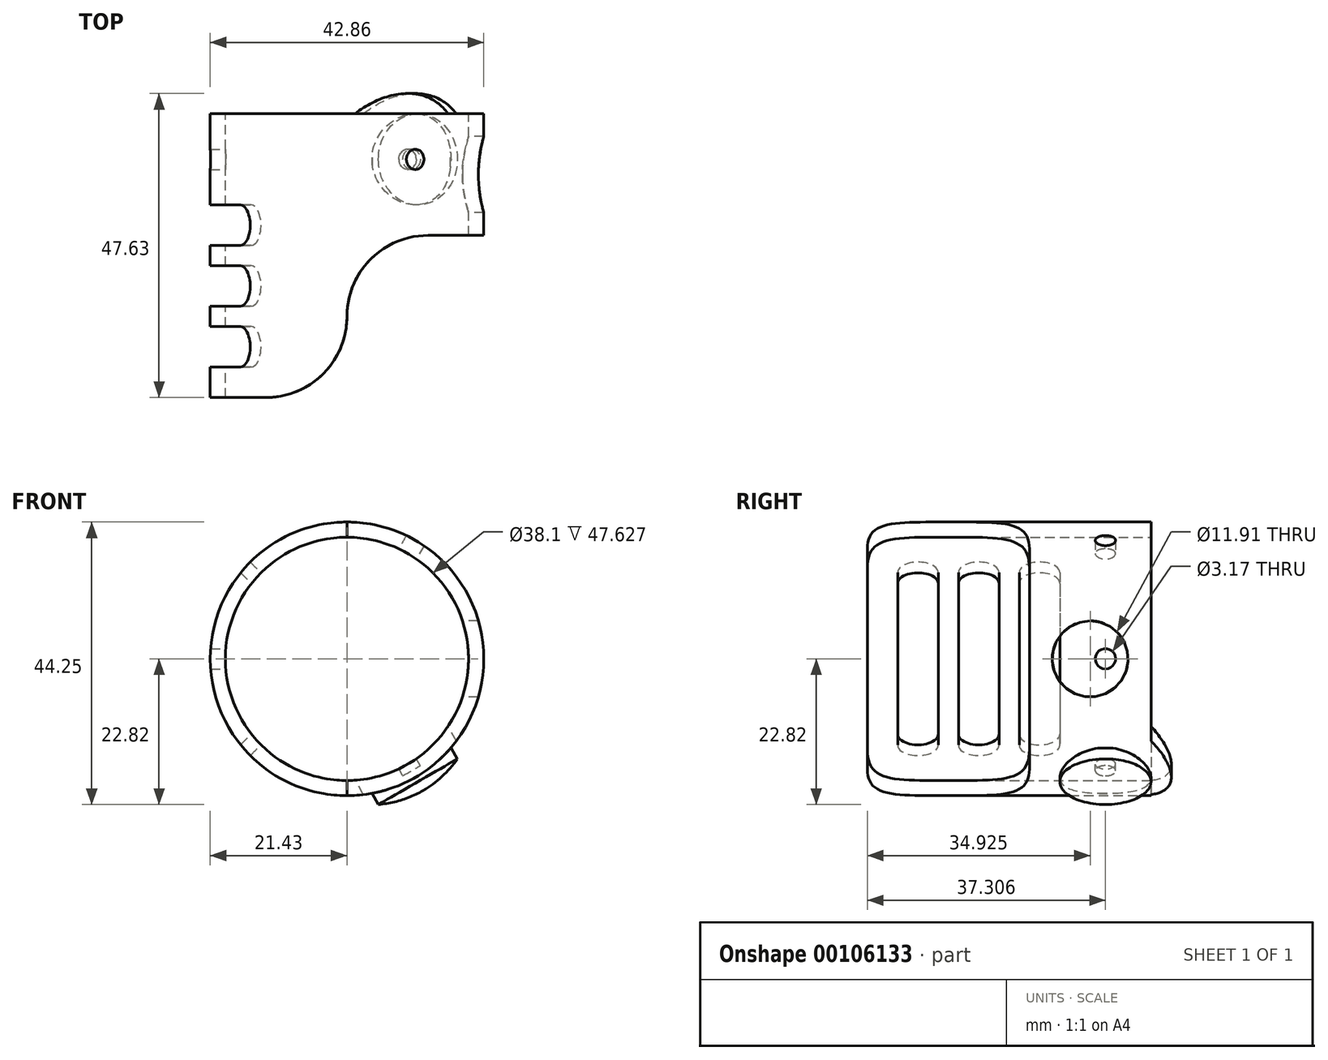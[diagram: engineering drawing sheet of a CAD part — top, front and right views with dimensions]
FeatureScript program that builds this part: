
annotation { "Feature Type Name" : "Feature", "Feature Type Description" : "" }
export const myFeature = defineFeature(function(context is Context, id is Id, definition is map)
    precondition{}
    {
        {
            var Q0;
            Q0=qCreatedBy(makeId("Right.planeOp"),FACE);
            var sketch = newSketch(context, id + "F0", { "sketchPlane" : qUnion([Q0])});
            skLineSegment(sketch, "E0", {"start": v(0, 0) * mm, "end": v(-152.4, 0) * mm, "construction": true});
            skLineSegment(sketch, "E1.bottom", {"start": v(-95.25, 21.43) * mm, "end": v(-47.63, 21.43) * mm});
            skLineSegment(sketch, "E1.top", {"start": v(-95.25, 19.05) * mm, "end": v(-47.63, 19.05) * mm});
            skLineSegment(sketch, "E1.left", {"start": v(-95.25, 21.43) * mm, "end": v(-95.25, 19.05) * mm});
            skLineSegment(sketch, "E1.right", {"start": v(-47.63, 21.43) * mm, "end": v(-47.63, 19.05) * mm});
            skSolve(sketch);
        }
        {
            var Q0;
            Q0 = qSketchRegion(id + "F0", true);
            var Q1;
            Q1=sQuery(id+"F0.wireOp",EDGE,"E0");
            revolve(context, id + "F1", {"entities" : qUnion([Q0]), "axis" : qUnion([Q1]), "revolveType" : RevolveType.FULL});
        }
        {
            var Q0;
            Q0=qCreatedBy(makeId("Top.planeOp"),FACE);
            var sketch = newSketch(context, id + "F2", { "sketchPlane" : qUnion([Q0])});
            skLineSegment(sketch, "E2", {"start": v(0, -95.25) * mm, "end": v(0, -82.55) * mm, "construction": true});
            skLineSegment(sketch, "E3", {"start": v(0, -82.55) * mm, "end": v(-12.7, -82.55) * mm, "construction": true});
            skArc(sketch, "E4", {"start": v(-12.7, -95.25) * mm, "mid": v(-3.72, -91.53) * mm, "end": v(0, -82.55) * mm});
            skLineSegment(sketch, "E5", {"start": v(-12.7, -95.25) * mm, "end": v(21.43, -95.25) * mm});
            skLineSegment(sketch, "E6", {"start": v(21.43, -95.25) * mm, "end": v(21.43, -69.85) * mm});
            skArc(sketch, "E7.MirrorC", {"start": v(0, -82.55) * mm, "mid": v(3.72, -73.57) * mm, "end": v(12.7, -69.85) * mm});
            skLineSegment(sketch, "E8", {"start": v(21.43, -69.85) * mm, "end": v(12.7, -69.85) * mm});
            skSolve(sketch);
        }
        {
            var Q0;
            Q0 = qSketchRegion(id + "F2", true);
            extrude(context, id + "F3", {"entities" : qUnion([Q0]), "operationType" : NewBodyOperationType.REMOVE, "endBound" : BoundingType.THROUGH_ALL, "oppositeDirection" : true, "depth" : 21.43 * mm, "hasSecondDirection" : true, "secondDirectionBound" : BoundingType.THROUGH_ALL, "secondDirectionOppositeDirection" : false, "secondDirectionDepth" : 25.4 * mm});
        }
        {
            var Q0;
            Q0=qCreatedBy(makeId("Right.planeOp"),FACE);
            var sketch = newSketch(context, id + "F4", { "sketchPlane" : qUnion([Q0])});
            skLineSegment(sketch, "E9", {"start": v(0, 0) * mm, "end": v(-60.32, 0) * mm, "construction": true});
            skCircle(sketch, "E10", {"center": v(-60.32, 0) * mm, "radius": 5.95 * mm});
            skSolve(sketch);
        }
        {
            var Q0;
            Q0 = qSketchRegion(id + "F4", true);
            var Q1;
            Q1=makeQuery(id+"F1.opRevolve","SWEPT_FACE",FACE,{"disambiguationData":[OSD([sQuery(id+"F0.wireOp",EDGE,"E1.bottom")])]});
            extrude(context, id + "F5", {"entities" : qUnion([Q0]), "operationType" : NewBodyOperationType.REMOVE, "endBound" : BoundingType.UP_TO_SURFACE, "endBoundEntityFace" : qUnion([Q1]), "depth" : 25.4 * mm});
        }
        {
            var Q0;
            Q0=qCreatedBy(makeId("Right.planeOp"),FACE);
            var sketch = newSketch(context, id + "F6", { "sketchPlane" : qUnion([Q0])});
            skLineSegment(sketch, "E11", {"start": v(0, 0) * mm, "end": v(-57.94, 0) * mm, "construction": true});
            skCircle(sketch, "E12", {"center": v(-57.94, 0) * mm, "radius": 1.59 * mm});
            skSolve(sketch);
        }
        {
            var Q0;
            Q0 = qSketchRegion(id + "F6", true);
            var Q1;
            Q1=makeQuery(id+"F1.opRevolve","SWEPT_FACE",FACE,{"disambiguationData":[OSD([sQuery(id+"F0.wireOp",EDGE,"E1.bottom")])]});
            extrude(context, id + "F7", {"entities" : qUnion([Q0]), "operationType" : NewBodyOperationType.REMOVE, "endBound" : BoundingType.UP_TO_SURFACE, "oppositeDirection" : true, "endBoundEntityFace" : qUnion([Q1]), "depth" : 25.4 * mm});
        }
        {
            var Q0;
            Q0=qCreatedBy(makeId("Front.planeOp"),FACE);
            var sketch = newSketch(context, id + "F8", { "sketchPlane" : qUnion([Q0])});
            skLineSegment(sketch, "E13", {"start": v(-21.43, 0) * mm, "end": v(21.43, 0) * mm, "construction": true});
            skLineSegment(sketch, "E14", {"start": v(0, 21.43) * mm, "end": v(0, -21.43) * mm, "construction": true});
            skLineSegment(sketch, "E15", {"start": v(-18.56, -10.72) * mm, "end": v(18.56, 10.72) * mm, "construction": true});
            skLineSegment(sketch, "E16.MirrorCS", {"start": v(18.56, -10.72) * mm, "end": v(-18.56, 10.72) * mm, "construction": true});
            skSolve(sketch);
        }
        {
            var Q0;
            Q0=sQuery(id+"F8.wireOp",VERTEX,"E15.end");
            var Q1;
            Q1=sQuery(id+"F8.wireOp",VERTEX,"E15.start");
            var Q2;
            Q2=sQuery(id+"F0.wireOp",VERTEX,"E0.end");
            cPlane(context, id + "F9", {"entities" : qUnion([Q0, Q1, Q2]), "cplaneType" : CPlaneType.THREE_POINT, "offset" : 25.4 * mm, "width" : 152.4 * mm, "height" : 152.4 * mm});
        }
        {
            var Q0;
            Q0=sQuery(id+"F8.wireOp",VERTEX,"E16.MirrorCS.end");
            var Q1;
            Q1=sQuery(id+"F8.wireOp",VERTEX,"E16.MirrorCS.start");
            var Q2;
            Q2=sQuery(id+"F0.wireOp",VERTEX,"E0.end");
            cPlane(context, id + "F10", {"entities" : qUnion([Q0, Q1, Q2]), "cplaneType" : CPlaneType.THREE_POINT, "offset" : 25.4 * mm, "width" : 152.4 * mm, "height" : 152.4 * mm});
        }
        {
            var Q0;
            Q0=qCreatedBy(id+"F9.planeOp",FACE);
            var sketch = newSketch(context, id + "F11", { "sketchPlane" : qUnion([Q0])});
            skLineSegment(sketch, "E17", {"start": v(0, 0) * mm, "end": v(0, 57.94) * mm, "construction": true});
            skCircle(sketch, "E18", {"center": v(0, 57.94) * mm, "radius": 1.59 * mm});
            skSolve(sketch);
        }
        {
            var Q0;
            Q0 = qSketchRegion(id + "F11", true);
            var Q1;
            Q1=makeQuery(id+"F1.opRevolve","SWEPT_FACE",FACE,{"disambiguationData":[OSD([sQuery(id+"F0.wireOp",EDGE,"E1.bottom")])]});
            extrude(context, id + "F12", {"entities" : qUnion([Q0]), "operationType" : NewBodyOperationType.REMOVE, "endBound" : BoundingType.UP_TO_SURFACE, "endBoundEntityFace" : qUnion([Q1]), "depth" : 25.4 * mm});
        }
        {
            var Q0;
            Q0=qCreatedBy(id+"F10.planeOp",FACE);
            var sketch = newSketch(context, id + "F13", { "sketchPlane" : qUnion([Q0])});
            skLineSegment(sketch, "E19", {"start": v(0, 0) * mm, "end": v(0, -57.94) * mm, "construction": true});
            skCircle(sketch, "E20", {"center": v(0, -57.94) * mm, "radius": 1.59 * mm});
            skSolve(sketch);
        }
        {
            var Q0;
            Q0 = qSketchRegion(id + "F13", true);
            var Q1;
            Q1=makeQuery(id+"F1.opRevolve","SWEPT_FACE",FACE,{"disambiguationData":[OSD([sQuery(id+"F0.wireOp",EDGE,"E1.bottom")])]});
            extrude(context, id + "F14", {"entities" : qUnion([Q0]), "operationType" : NewBodyOperationType.REMOVE, "endBound" : BoundingType.UP_TO_SURFACE, "endBoundEntityFace" : qUnion([Q1]), "depth" : 25.4 * mm});
        }
        {
            var Q0;
            Q0=qCreatedBy(id+"F9.planeOp",FACE);
            var sketch = newSketch(context, id + "F15", { "sketchPlane" : qUnion([Q0])});
            skLineSegment(sketch, "E21", {"start": v(0, 0) * mm, "end": v(0, 60.32) * mm, "construction": true});
            skArc(sketch, "E22", {"start": v(-8.4, 50.8) * mm, "mid": v(0, 47.62) * mm, "end": v(8.4, 50.8) * mm});
            skLineSegment(sketch, "E23", {"start": v(8.4, 50.8) * mm, "end": v(21.43, 50.8) * mm});
            skLineSegment(sketch, "E24", {"start": v(21.43, 50.8) * mm, "end": v(21.43, 47.63) * mm});
            skLineSegment(sketch, "E25", {"start": v(21.43, 47.63) * mm, "end": v(-21.43, 47.62) * mm});
            skLineSegment(sketch, "E26.MirrorCS", {"start": v(-21.43, 50.8) * mm, "end": v(-21.43, 47.63) * mm});
            skLineSegment(sketch, "E27.MirrorCS", {"start": v(-8.4, 50.8) * mm, "end": v(-21.43, 50.8) * mm});
            skSolve(sketch);
        }
        {
            var Q0;
            Q0 = qSketchRegion(id + "F15", true);
            var Q1;
            Q1=makeQuery(id+"F1.opRevolve","SWEPT_FACE",FACE,{"disambiguationData":[OSD([sQuery(id+"F0.wireOp",EDGE,"E1.bottom")])]});
            extrude(context, id + "F16", {"entities" : qUnion([Q0]), "operationType" : NewBodyOperationType.REMOVE, "endBoundEntityFace" : qUnion([Q1]), "depth" : 21.43 * mm});
        }
        {
            var Q0;
            Q0=qCreatedBy(id+"F9.planeOp",FACE);
            var sketch = newSketch(context, id + "F17", { "sketchPlane" : qUnion([Q0])});
            skLineSegment(sketch, "E28.bottom", {"start": v(21.43, 50.8) * mm, "end": v(-21.43, 50.8) * mm});
            skLineSegment(sketch, "E28.top", {"start": v(21.43, 47.63) * mm, "end": v(-21.43, 47.63) * mm});
            skLineSegment(sketch, "E28.left", {"start": v(21.43, 50.8) * mm, "end": v(21.43, 47.63) * mm});
            skLineSegment(sketch, "E28.right", {"start": v(-21.43, 50.8) * mm, "end": v(-21.43, 47.63) * mm});
            skSolve(sketch);
        }
        {
            var Q0;
            Q0 = qSketchRegion(id + "F17", true);
            extrude(context, id + "F18", {"entities" : qUnion([Q0]), "operationType" : NewBodyOperationType.REMOVE, "oppositeDirection" : true, "depth" : 21.43 * mm});
        }
        {
            var Q0;
            Q0=qCreatedBy(id+"F9.planeOp",FACE);
            cPlane(context, id + "F19", {"entities" : qUnion([Q0]), "cplaneType" : CPlaneType.OFFSET, "offset" : 21.43 * mm, "width" : 152.4 * mm, "height" : 152.4 * mm});
        }
        {
            var Q0;
            Q0=qCreatedBy(id+"F19.planeOp",FACE);
            var sketch = newSketch(context, id + "F20", { "sketchPlane" : qUnion([Q0])});
            skLineSegment(sketch, "E29", {"start": v(0, 0) * mm, "end": v(0, 57.94) * mm, "construction": true});
            skCircle(sketch, "E30", {"center": v(0, 57.94) * mm, "radius": 7.14 * mm});
            skSolve(sketch);
        }
        {
            var Q0;
            Q0 = qSketchRegion(id + "F20", true);
            var Q1;
            Q1=makeQuery(id+"F1.opRevolve","SWEPT_FACE",FACE,{"disambiguationData":[OSD([sQuery(id+"F0.wireOp",EDGE,"E1.bottom")])]});
            extrude(context, id + "F21", {"entities" : qUnion([Q0]), "operationType" : NewBodyOperationType.ADD, "endBoundEntityFace" : qUnion([Q1]), "depth" : 0.8 * mm, "hasSecondDirection" : true, "secondDirectionOppositeDirection" : true, "secondDirectionDepth" : 1.2 * mm});
        }
        {
            var Q0;
            Q0=qCreatedBy(makeId("Front.planeOp"),FACE);
            cPlane(context, id + "F22", {"entities" : qUnion([Q0]), "cplaneType" : CPlaneType.OFFSET, "offset" : 57.94 * mm, "width" : 152.4 * mm, "height" : 152.4 * mm});
        }
        {
            var Q0;
            Q0=qCreatedBy(id+"F22.planeOp",FACE);
            var sketch = newSketch(context, id + "F23", { "sketchPlane" : qUnion([Q0])});
            skLineSegment(sketch, "E31", {"start": v(0, 0) * mm, "end": v(21.43, 0) * mm, "construction": true});
            skLineSegment(sketch, "E32", {"start": v(0, 0) * mm, "end": v(11.11, -19.25) * mm, "construction": true});
            skLineSegment(sketch, "E33", {"start": v(11.11, -19.25) * mm, "end": v(17.3, -15.68) * mm});
            skArc(sketch, "E34", {"start": v(11.92, -20.64) * mm, "mid": v(14.88, -18.46) * mm, "end": v(17.3, -15.68) * mm});
            skLineSegment(sketch, "E35", {"start": v(11.11, -19.25) * mm, "end": v(11.92, -20.64) * mm});
            skSolve(sketch);
        }
        {
            var Q0;
            Q0 = qSketchRegion(id + "F23", true);
            var Q1;
            Q1=sQuery(id+"F23.wireOp",EDGE,"E32");
            revolve(context, id + "F24", {"operationType" : NewBodyOperationType.ADD, "entities" : qUnion([Q0]), "axis" : qUnion([Q1]), "revolveType" : RevolveType.FULL});
        }
        {
            var Q0;
            Q0=qCreatedBy(makeId("Right.planeOp"),FACE);
            cPlane(context, id + "F25", {"entities" : qUnion([Q0]), "cplaneType" : CPlaneType.OFFSET, "offset" : 21.43 * mm, "oppositeDirection" : true, "width" : 152.4 * mm, "height" : 152.4 * mm});
        }
        {
            var Q0;
            Q0=qCreatedBy(makeId("Right.planeOp"),FACE);
            cPlane(context, id + "F26", {"entities" : qUnion([Q0]), "cplaneType" : CPlaneType.OFFSET, "offset" : 8.73 * mm, "oppositeDirection" : true, "width" : 152.4 * mm, "height" : 152.4 * mm});
        }
        {
            var Q0;
            Q0=qCreatedBy(id+"F25.planeOp",FACE);
            var sketch = newSketch(context, id + "F27", { "sketchPlane" : qUnion([Q0])});
            skLineSegment(sketch, "E36", {"start": v(0, 0) * mm, "end": v(-87.31, 0) * mm, "construction": true});
            skLineSegment(sketch, "E37", {"start": v(-87.31, 18.26) * mm, "end": v(-87.31, -18.26) * mm, "construction": true});
            skLineSegment(sketch, "E38", {"start": v(-77.79, 18.26) * mm, "end": v(-77.79, -18.26) * mm, "construction": true});
            skLineSegment(sketch, "E39", {"start": v(-68.26, 18.26) * mm, "end": v(-68.26, -18.26) * mm, "construction": true});
            skArc(sketch, "E40", {"start": v(-84.14, 18.26) * mm, "mid": v(-87.31, 21.43) * mm, "end": v(-90.49, 18.26) * mm});
            skArc(sketch, "E41", {"start": v(-74.61, 18.26) * mm, "mid": v(-77.79, 21.43) * mm, "end": v(-80.96, 18.26) * mm});
            skArc(sketch, "E42", {"start": v(-65.09, 18.26) * mm, "mid": v(-68.26, 21.43) * mm, "end": v(-71.44, 18.26) * mm});
            skArc(sketch, "E43.MirrorC", {"start": v(-65.09, -18.26) * mm, "mid": v(-68.26, -21.43) * mm, "end": v(-71.44, -18.26) * mm});
            skArc(sketch, "E44.MirrorC", {"start": v(-74.61, -18.26) * mm, "mid": v(-77.79, -21.43) * mm, "end": v(-80.96, -18.26) * mm});
            skArc(sketch, "E45.MirrorC", {"start": v(-84.14, -18.26) * mm, "mid": v(-87.31, -21.43) * mm, "end": v(-90.49, -18.26) * mm});
            skLineSegment(sketch, "E46", {"start": v(-65.09, 18.26) * mm, "end": v(-65.09, -18.26) * mm});
            skLineSegment(sketch, "E47", {"start": v(-71.44, 18.26) * mm, "end": v(-71.44, -18.26) * mm});
            skLineSegment(sketch, "E48", {"start": v(-74.61, 18.26) * mm, "end": v(-74.61, -18.26) * mm});
            skLineSegment(sketch, "E49", {"start": v(-80.96, 18.26) * mm, "end": v(-80.96, -18.26) * mm});
            skLineSegment(sketch, "E50", {"start": v(-84.14, 18.26) * mm, "end": v(-84.14, -18.26) * mm});
            skLineSegment(sketch, "E51", {"start": v(-90.49, 18.26) * mm, "end": v(-90.49, -18.26) * mm});
            skSolve(sketch);
        }
        {
            var Q0;
            Q0=qCreatedBy(id+"F26.planeOp",FACE);
            var sketch = newSketch(context, id + "F28", { "sketchPlane" : qUnion([Q0])});
            skLineSegment(sketch, "E52", {"start": v(0, 0) * mm, "end": v(-87.31, 0) * mm, "construction": true});
            skLineSegment(sketch, "E53", {"start": v(-87.31, 5.56) * mm, "end": v(-87.31, -5.56) * mm, "construction": true});
            skLineSegment(sketch, "E54", {"start": v(-77.79, 5.56) * mm, "end": v(-77.79, -5.56) * mm, "construction": true});
            skLineSegment(sketch, "E55", {"start": v(-68.26, 5.56) * mm, "end": v(-68.26, -5.56) * mm, "construction": true});
            skArc(sketch, "E56", {"start": v(-65.09, 5.56) * mm, "mid": v(-68.26, 8.73) * mm, "end": v(-71.44, 5.56) * mm});
            skArc(sketch, "E57", {"start": v(-74.61, 5.56) * mm, "mid": v(-77.79, 8.73) * mm, "end": v(-80.96, 5.56) * mm});
            skArc(sketch, "E58", {"start": v(-84.14, 5.56) * mm, "mid": v(-87.31, 8.73) * mm, "end": v(-90.49, 5.56) * mm});
            skArc(sketch, "E59.MirrorC", {"start": v(-84.14, -5.56) * mm, "mid": v(-87.31, -8.73) * mm, "end": v(-90.49, -5.56) * mm});
            skArc(sketch, "E60.MirrorC", {"start": v(-74.61, -5.56) * mm, "mid": v(-77.79, -8.73) * mm, "end": v(-80.96, -5.56) * mm});
            skArc(sketch, "E61.MirrorC", {"start": v(-65.09, -5.56) * mm, "mid": v(-68.26, -8.73) * mm, "end": v(-71.44, -5.56) * mm});
            skLineSegment(sketch, "E62", {"start": v(-65.09, 5.56) * mm, "end": v(-65.09, -5.56) * mm});
            skLineSegment(sketch, "E63", {"start": v(-71.44, 5.56) * mm, "end": v(-71.44, -5.56) * mm});
            skLineSegment(sketch, "E64", {"start": v(-74.61, 5.56) * mm, "end": v(-74.61, -5.56) * mm});
            skLineSegment(sketch, "E65", {"start": v(-80.96, 5.56) * mm, "end": v(-80.96, -5.56) * mm});
            skLineSegment(sketch, "E66", {"start": v(-84.14, 5.56) * mm, "end": v(-84.14, -5.56) * mm});
            skLineSegment(sketch, "E67", {"start": v(-90.49, 5.56) * mm, "end": v(-90.49, -5.56) * mm});
            skSolve(sketch);
        }
        {
            var Q1;
            Q1=makeQuery(id+"F27.imprint","IMPRINT",FACE,{"disambiguationData":[TD([[makeQuery(id+"F27.imprint","IMPRINT",EDGE,{"derivedFrom":sQuery(id+"F27.wireOp",EDGE,"E40")}),1.0]])]});
            var Q2;
            Q2=makeQuery(id+"F28.imprint","IMPRINT",FACE,{"disambiguationData":[TD([[makeQuery(id+"F28.imprint","IMPRINT",EDGE,{"derivedFrom":sQuery(id+"F28.wireOp",EDGE,"E58")}),1.0]])]});
            loft(context, id + "F29", {"operationType" : NewBodyOperationType.REMOVE, "sheetProfilesArray" : [{ "sheetProfileEntities" : qUnion([Q1]) }, { "sheetProfileEntities" : qUnion([Q2]) }]});
        }
        {
            var Q0;
            Q0=makeQuery(id+"F27.imprint","IMPRINT",FACE,{"disambiguationData":[TD([[makeQuery(id+"F27.imprint","IMPRINT",EDGE,{"derivedFrom":sQuery(id+"F27.wireOp",EDGE,"E41")}),1.0]])]});
            var Q1;
            Q1=makeQuery(id+"F28.imprint","IMPRINT",FACE,{"disambiguationData":[TD([[makeQuery(id+"F28.imprint","IMPRINT",EDGE,{"derivedFrom":sQuery(id+"F28.wireOp",EDGE,"E57")}),1.0]])]});
            loft(context, id + "F30", {"operationType" : NewBodyOperationType.REMOVE, "sheetProfilesArray" : [{ "sheetProfileEntities" : qUnion([Q0]) }, { "sheetProfileEntities" : qUnion([Q1]) }]});
        }
        {
            var Q0;
            Q0=makeQuery(id+"F27.imprint","IMPRINT",FACE,{"disambiguationData":[TD([[makeQuery(id+"F27.imprint","IMPRINT",EDGE,{"derivedFrom":sQuery(id+"F27.wireOp",EDGE,"E42")}),1.0]])]});
            var Q1;
            Q1=makeQuery(id+"F28.imprint","IMPRINT",FACE,{"disambiguationData":[TD([[makeQuery(id+"F28.imprint","IMPRINT",EDGE,{"derivedFrom":sQuery(id+"F28.wireOp",EDGE,"E56")}),1.0]])]});
            loft(context, id + "F31", {"operationType" : NewBodyOperationType.REMOVE, "sheetProfilesArray" : [{ "sheetProfileEntities" : qUnion([Q0]) }, { "sheetProfileEntities" : qUnion([Q1]) }]});
        }
    });
